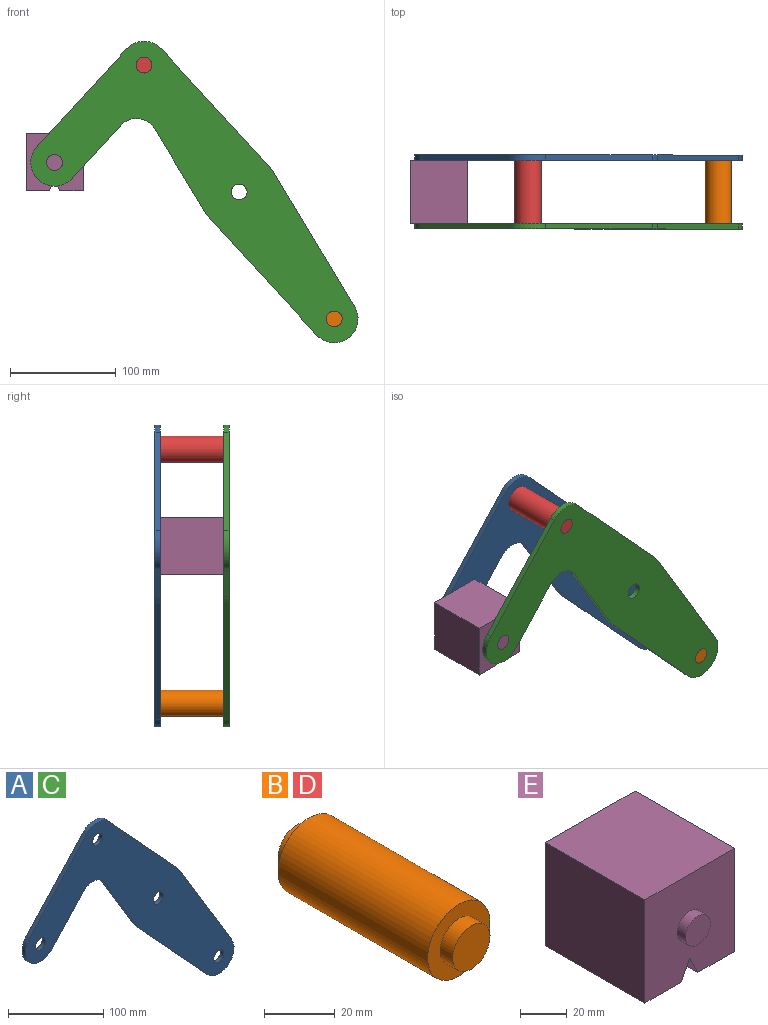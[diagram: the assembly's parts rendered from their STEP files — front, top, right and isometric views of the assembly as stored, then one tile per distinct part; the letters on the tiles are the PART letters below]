
ASSEMBLY  parts=5 mates=3
PART A: 18 faces, bbox 309.5x5x285.1 mm
  f0: cylinder r=22.5mm len=39.07mm, axis (0,1,0), area 353.4mm2, adj f1,f13,f16,f17
  f1: plane 50.28x46.21mm, normal (0.74,0,-0.68), area 341.4mm2, adj f0,f2,f16,f17
  f2: cylinder r=20mm len=31.85mm, axis (0,1,0), area 185.5mm2, adj f1,f3,f16,f17
  f3: plane 79.23x47.81mm, normal (-0.86,0,-0.52), area 462.7mm2, adj f2,f4,f16,f17
  f4: cylinder r=37.5mm len=6mm, axis (0,1,0), area 37.6mm2, adj f3,f5,f16,f17
  f5: plane 109.88x101mm, normal (-0.74,0,-0.68), area 746.2mm2, adj f4,f6,f16,f17
  f6: cylinder r=22.5mm len=39.07mm, axis (0,1,0), area 330.9mm2, adj f5,f7,f16,f17
  f7: plane 127.78x77.11mm, normal (0.86,0,0.52), area 746.2mm2, adj f6,f8,f16,f17
  f8: cylinder r=37.5mm len=6mm, axis (0,1,0), area 37.6mm2, adj f7,f9,f16,f17
  f9: plane 109.88x101mm, normal (0.74,0,0.68), area 746.2mm2, adj f8,f10,f16,f17
  f10: cylinder r=22.5mm len=33.13mm, axis (0,1,0), area 186.2mm2, adj f9,f13,f16,f17
  f11: cylinder r=7.5mm len=15mm, axis (0,1,0), area 235.6mm2, adj f16,f17
  f12: cylinder r=7.5mm len=15mm, axis (0,1,0), area 235.6mm2, adj f16,f17
  f13: plane 92.03x84.59mm, normal (-0.74,0,0.68), area 625mm2, adj f0,f10,f16,f17
  f14: cylinder r=7.5mm len=15mm, axis (0,1,0), area 235.6mm2, adj f16,f17
  f15: cylinder r=7.5mm len=15mm, axis (0,1,0), area 235.6mm2, adj f16,f17
  f16: plane 309.5x285.07mm, normal (0,-1,0), area 24555.4mm2, adj f0,f1,f2,f3,f4,f5,f6,f7
  f17: plane 309.5x285.07mm, normal (0,1,0), area 24555.4mm2, adj f0,f1,f2,f3,f4,f5,f6,f7
PART B: 7 faces, bbox 25x70x25 mm
  f0: cylinder r=12.5mm len=60mm, axis (0,-1,0), area 4712.4mm2, adj f2,f5
  f1: cylinder r=7.5mm len=15mm, axis (0,1,0), area 235.6mm2, adj f2,f3
  f2: plane 25x25mm, normal (0,-1,0), area 314.2mm2, adj f0,f1
  f3: plane 15x15mm, normal (0,-1,0), area 176.7mm2, adj f1
  f4: cylinder r=7.5mm len=15mm, axis (0,-1,0), area 235.6mm2, adj f5,f6
  f5: plane 25x25mm, normal (0,1,0), area 314.2mm2, adj f0,f4
  f6: plane 15x15mm, normal (0,1,0), area 176.7mm2, adj f4
PART C: same geometry as A
PART D: same geometry as B
PART E: 13 faces, bbox 54x70x54 mm
  f0: plane 60x54.01mm, normal (-1,0,0), area 3240.4mm2, adj f1,f6,f7,f10
  f1: plane 60x54.01mm, normal (0,0,1), area 3240.4mm2, adj f0,f2,f7,f10
  f2: plane 60x54.01mm, normal (1,0,0), area 3240.4mm2, adj f1,f3,f7,f10
  f3: plane 60x22mm, normal (0,0,-1), area 1320.2mm2, adj f2,f4,f7,f10
  f4: plane 60x10mm, normal (-0.89,0,-0.45), area 670.8mm2, adj f3,f5,f7,f10
  f5: plane 60x10mm, normal (0.89,0,-0.45), area 670.8mm2, adj f4,f6,f7,f10
  f6: plane 60x22mm, normal (0,0,-1), area 1320.2mm2, adj f0,f5,f7,f10
  f7: plane 54.01x54.01mm, normal (0,-1,0), area 2690mm2, adj f0,f1,f2,f3,f4,f5,f6,f9
  f8: plane 15x15mm, normal (0,-1,0), area 176.7mm2, adj f9
  f9: cylinder r=7.5mm len=15mm, axis (0,1,0), area 235.6mm2, adj f7,f8
  f10: plane 54.01x54.01mm, normal (0,1,0), area 2690mm2, adj f0,f1,f2,f3,f4,f5,f6,f12
  f11: plane 15x15mm, normal (0,1,0), area 176.7mm2, adj f12
  f12: cylinder r=7.5mm len=15mm, axis (0,-1,0), area 235.6mm2, adj f10,f11
PLACE A t=(0,35,0)mm
PLACE B t=(179.91,-30,-240.07)mm
PLACE C t=(0,-30,0)mm fixed
PLACE D t=(0,-30,0)mm
PLACE E t=(0,-30,0)mm
MATE revolute E.f9 <-> C.f0  axis (0,-1,0) through (-174.54,-30,28)mm
MATE fastened B.f0 <-> C.f6  axis (0,1,0) through (89.96,-30,-120.03)mm
MATE fastened A.f10 <-> D.f0  axis (0,-1,0) through (-89.96,30,120.03)mm
